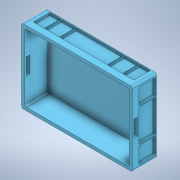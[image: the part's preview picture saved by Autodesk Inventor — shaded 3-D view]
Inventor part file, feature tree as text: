
AUTODESK INVENTOR PART (.ipt)
format: ipt  version: 2020 (Build 240168000, 168)  size: 264,704 bytes
history: native  units: in
note: dims shown in document units (in); Inventor stores cm internally (conversion verified against a paired STEP export)
features: extrude x1, sketch x1, other x1
ambient origin geometry x8: Origin, YZ Plane, XZ Plane, XY Plane, X Axis, Y Axis, Z Axis, Center Point
bodies: Solid1 (feature_tree)
feature tree (3):
  extrude  "Extrusion1"  Depth=3.5433in
  sketch  "Sketch1"  dims[d0=0.7874in d1=3.5433in d2=0.2756in d3=29.6063in d4=0.0in]
  other  "Plastic crate 600x400x120_1_1:1"
